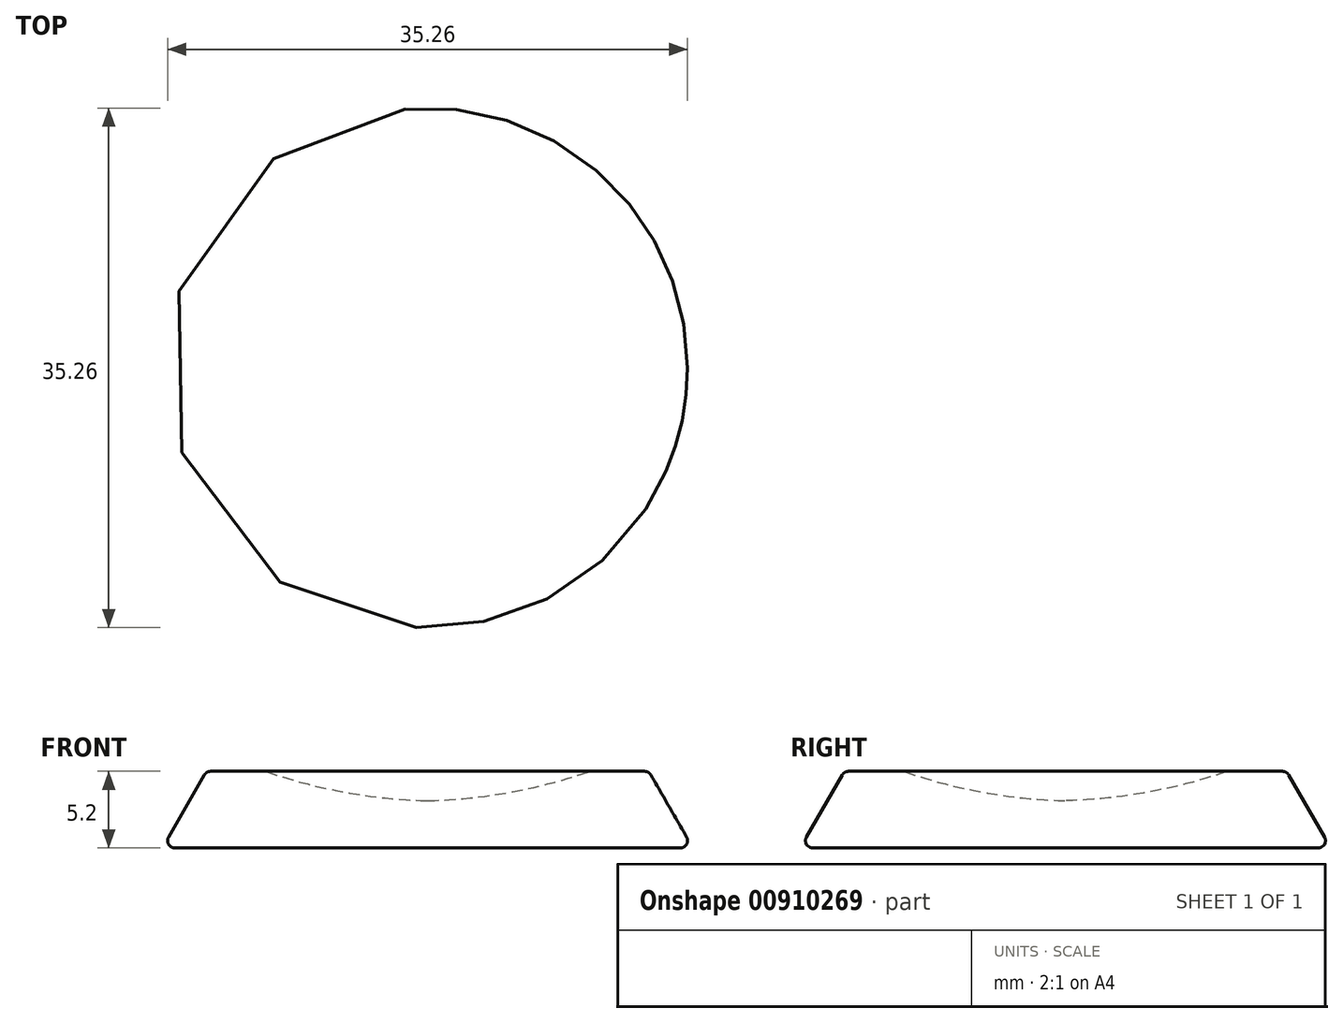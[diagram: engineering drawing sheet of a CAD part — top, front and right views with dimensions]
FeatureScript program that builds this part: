
annotation { "Feature Type Name" : "Feature", "Feature Type Description" : "" }
export const myFeature = defineFeature(function(context is Context, id is Id, definition is map)
    precondition{}
    {
        {
            var Q0;
            Q0=qCreatedBy(makeId("Front.planeOp"),FACE);
            var sketch = newSketch(context, id + "F0", { "sketchPlane" : qUnion([Q0])});
            skArc(sketch, "E0", {"start": v(0, -2) * mm, "mid": v(5.58, -1.42) * mm, "end": v(11, 0) * mm});
            skLineSegment(sketch, "E1", {"start": v(11, 0) * mm, "end": v(15, 0) * mm});
            skLineSegment(sketch, "E2", {"start": v(15, 0) * mm, "end": v(18, -5.2) * mm});
            skLineSegment(sketch, "E3", {"start": v(18, -5.2) * mm, "end": v(0, -5.2) * mm});
            skLineSegment(sketch, "E4", {"start": v(0, -5.2) * mm, "end": v(0, -2) * mm});
            skSolve(sketch);
        }
        {
            var Q0;
            Q0=makeQuery(id+"F0.imprint","IMPRINT",FACE,{"disambiguationData":[TD([[makeQuery(id+"F0.imprint","IMPRINT",EDGE,{"derivedFrom":sQuery(id+"F0.wireOp",EDGE,"E0")}),-1.0]])]});
            var Q1;
            Q1=sQuery(id+"F0.wireOp",EDGE,"E4");
            revolve(context, id + "F1", {"surfaceOperationType" : NewSurfaceOperationType.NEW, "entities" : qUnion([Q0]), "axis" : qUnion([Q1]), "revolveType" : RevolveType.FULL});
        }
        {
            var Q0;
            Q0=makeQuery(id+"F1.opRevolve","SWEPT_EDGE",EDGE,{"disambiguationData":[OSD([sQuery(id+"F0.wireOp",EDGE,"E2"),sQuery(id+"F0.wireOp",EDGE,"E3")])]});
            var Q1;
            Q1=makeQuery(id+"F1.opRevolve","SWEPT_EDGE",EDGE,{"disambiguationData":[OSD([sQuery(id+"F0.wireOp",EDGE,"E0"),sQuery(id+"F0.wireOp",EDGE,"E1")])]});
            var Q2;
            Q2=makeQuery(id+"F1.opRevolve","SWEPT_EDGE",EDGE,{"disambiguationData":[OSD([sQuery(id+"F0.wireOp",EDGE,"E1"),sQuery(id+"F0.wireOp",EDGE,"E2")])]});
            fillet(context, id + "F2", {"entities" : qUnion([Q0, Q1, Q2]), "radius" : .5 * mm, "tangentPropagation" : true, "allowEdgeOverflow" : false});
        }
    });
